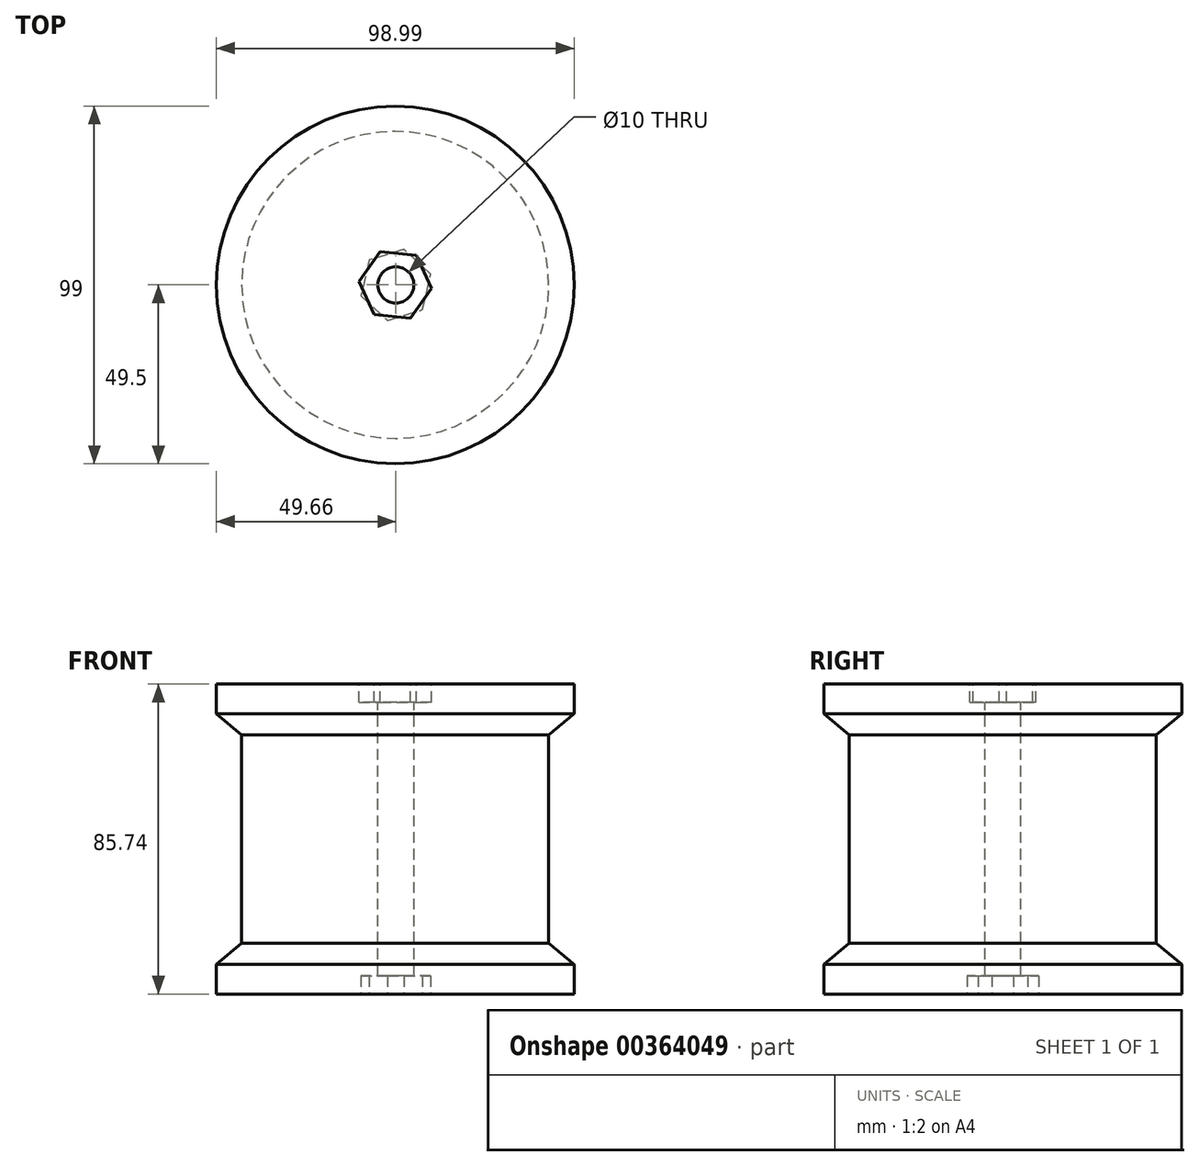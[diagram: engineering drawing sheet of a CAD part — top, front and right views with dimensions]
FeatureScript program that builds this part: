
annotation { "Feature Type Name" : "Feature", "Feature Type Description" : "" }
export const myFeature = defineFeature(function(context is Context, id is Id, definition is map)
    precondition{}
    {
        {
            var Q0;
            Q0=qCreatedBy(makeId("Front.planeOp"),FACE);
            var sketch = newSketch(context, id + "F0", { "sketchPlane" : qUnion([Q0])});
            skLineSegment(sketch, "E0", {"start": v(-0.16, 58.47) * mm, "end": v(-49.66, 58.47) * mm});
            skLineSegment(sketch, "E1", {"start": v(-49.66, 58.47) * mm, "end": v(-49.66, 50.29) * mm});
            skLineSegment(sketch, "E2", {"start": v(-49.66, 50.29) * mm, "end": v(-42.65, 44.44) * mm});
            skLineSegment(sketch, "E3", {"start": v(-42.65, 44.44) * mm, "end": v(-42.65, 15.6) * mm});
            skLineSegment(sketch, "E4", {"start": v(-0.16, 58.47) * mm, "end": v(-0.16, 15.6) * mm});
            skLineSegment(sketch, "E5.MirrorCS", {"start": v(-49.66, -19.09) * mm, "end": v(-42.65, -13.24) * mm});
            skLineSegment(sketch, "E6.MirrorCS", {"start": v(-49.66, -27.27) * mm, "end": v(-49.66, -19.09) * mm});
            skLineSegment(sketch, "E7.MirrorCS", {"start": v(-0.16, -27.27) * mm, "end": v(-49.66, -27.27) * mm});
            skLineSegment(sketch, "E8.MirrorCS", {"start": v(-0.16, -27.27) * mm, "end": v(-0.16, 15.6) * mm});
            skLineSegment(sketch, "E9.MirrorCS", {"start": v(-42.65, -13.24) * mm, "end": v(-42.65, 15.6) * mm});
            skLineSegment(sketch, "E10", {"start": v(-0.16, 58.47) * mm, "end": v(-0.16, -27.27) * mm});
            skSolve(sketch);
        }
        {
            var Q0;
            Q0=makeQuery(id+"F0.imprint","IMPRINT",FACE,{"disambiguationData":[TD([[makeQuery(id+"F0.imprint","IMPRINT",EDGE,{"derivedFrom":sQuery(id+"F0.wireOp",EDGE,"E0")}),1.0]])]});
            var Q1;
            Q1=sQuery(id+"F0.wireOp",EDGE,"E10");
            revolve(context, id + "F1", {"entities" : qUnion([Q0]), "axis" : qUnion([Q1]), "revolveType" : RevolveType.FULL});
        }
        {
            var Q0;
            Q0=qCreatedBy(makeId("Top.planeOp"),FACE);
            var sketch = newSketch(context, id + "F2", { "sketchPlane" : qUnion([Q0])});
            skCircle(sketch, "E11", {"center": v(0, 0) * mm, "radius": 5 * mm});
            skSolve(sketch);
        }
        {
            var Q0;
            Q0 = qSketchRegion(id + "F2", true);
            extrude(context, id + "F3", {"entities" : qUnion([Q0]), "operationType" : NewBodyOperationType.REMOVE, "endBound" : BoundingType.SYMMETRIC, "oppositeDirection" : true, "depth" : 1000 * mm});
        }
        {
            var Q0;
            Q0=makeQuery(id+"F1.opRevolve","SWEPT_FACE",FACE,{"disambiguationData":[OSD([sQuery(id+"F0.wireOp",EDGE,"E0")])]});
            var sketch = newSketch(context, id + "F4", { "sketchPlane" : qUnion([Q0])});
            skCircle(sketch, "E12.cCircle", {"center": v(-0.16, 0) * mm, "radius": 8.75 * mm, "construction": true});
            skLineSegment(sketch, "E12.0", {"start": v(-10.22, 0.98) * mm, "end": v(-4.35, 9.2) * mm});
            skLineSegment(sketch, "E12.1", {"start": v(-4.35, 9.2) * mm, "end": v(5.7, 8.22) * mm});
            skLineSegment(sketch, "E12.2", {"start": v(5.7, 8.22) * mm, "end": v(9.9, -0.98) * mm});
            skLineSegment(sketch, "E12.3", {"start": v(9.9, -0.98) * mm, "end": v(4.02, -9.2) * mm});
            skLineSegment(sketch, "E12.4", {"start": v(4.02, -9.2) * mm, "end": v(-6.04, -8.22) * mm});
            skLineSegment(sketch, "E12.5", {"start": v(-6.04, -8.22) * mm, "end": v(-10.22, 0.98) * mm});
            skPoint(sketch, "E12.0.midPoint", {"position": v(-7.29, 5.09) * mm});
            skSolve(sketch);
        }
        {
            var Q0;
            Q0=makeQuery(id+"F4.imprint","IMPRINT",FACE,{"disambiguationData":[TD([[makeQuery(id+"F4.imprint","IMPRINT",EDGE,{"derivedFrom":makeQuery(id+"F3.boolean.opBoolean","INTERSECT",EDGE,{"derivedFrom":[makeQuery(id+"F1.opRevolve","SWEPT_FACE",FACE,{"disambiguationData":[OSD([sQuery(id+"F0.wireOp",EDGE,"E0")])]}),makeQuery(id+"F3.opExtrude","SWEPT_FACE",FACE,{"disambiguationData":[OSD([sQuery(id+"F2.wireOp",EDGE,"E11")])]})]})}),1.0]])]});
            var Q1;
            Q1=makeQuery(id+"F4.imprint","IMPRINT",FACE,{"disambiguationData":[TD([[makeQuery(id+"F4.imprint","IMPRINT",EDGE,{"derivedFrom":sQuery(id+"F4.wireOp",EDGE,"E12.0")}),-1.0]])]});
            extrude(context, id + "F5", {"entities" : qUnion([Q0, Q1]), "operationType" : NewBodyOperationType.REMOVE, "oppositeDirection" : true, "depth" : 5 * mm});
        }
        {
            var Q0;
            Q0=makeQuery(id+"F1.opRevolve","SWEPT_FACE",FACE,{"disambiguationData":[OSD([sQuery(id+"F0.wireOp",EDGE,"E7.MirrorCS")])]});
            var sketch = newSketch(context, id + "F6", { "sketchPlane" : qUnion([Q0])});
            skCircle(sketch, "E13.cCircle", {"center": v(0, 0) * mm, "radius": 8.75 * mm, "construction": true});
            skLineSegment(sketch, "E13.0", {"start": v(9.65, -2.98) * mm, "end": v(2.24, -9.85) * mm});
            skLineSegment(sketch, "E13.1", {"start": v(2.24, -9.85) * mm, "end": v(-7.41, -6.87) * mm});
            skLineSegment(sketch, "E13.2", {"start": v(-7.41, -6.87) * mm, "end": v(-9.65, 2.98) * mm});
            skLineSegment(sketch, "E13.3", {"start": v(-9.65, 2.98) * mm, "end": v(-2.24, 9.85) * mm});
            skLineSegment(sketch, "E13.4", {"start": v(-2.24, 9.85) * mm, "end": v(7.41, 6.87) * mm});
            skLineSegment(sketch, "E13.5", {"start": v(7.41, 6.87) * mm, "end": v(9.65, -2.98) * mm});
            skPoint(sketch, "E13.0.midPoint", {"position": v(5.95, -6.42) * mm});
            skSolve(sketch);
        }
        {
            var Q0;
            Q0=makeQuery(id+"F6.imprint","IMPRINT",FACE,{"disambiguationData":[TD([[makeQuery(id+"F6.imprint","IMPRINT",EDGE,{"derivedFrom":sQuery(id+"F6.wireOp",EDGE,"E13.0")}),-1.0]])]});
            extrude(context, id + "F7", {"entities" : qUnion([Q0]), "operationType" : NewBodyOperationType.REMOVE, "oppositeDirection" : true, "depth" : 5 * mm});
        }
    });
